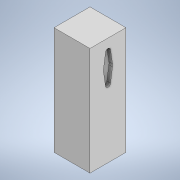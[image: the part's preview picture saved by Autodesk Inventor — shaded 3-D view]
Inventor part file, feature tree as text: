
AUTODESK INVENTOR PART (.ipt)
format: ipt  version: 2021 (Build 250183000, 183)  size: 110,080 bytes
history: native  units: mm
features: extrude x2, sketch x2
ambient origin geometry x8: Origin, YZ Plane, XZ Plane, XY Plane, X Axis, Y Axis, Z Axis, Center Point
bodies: Solid1 (feature_tree)
feature tree (4):
  extrude  "Extrusion1"  Depth=50.0mm
  extrude  "Extrusion2"  Depth=5.0mm
  sketch  "Sketch1"  dims[d0=50.0mm d1=50.0mm]
  sketch  "Sketch2"  dims[d2=150.0mm d3=0.0mm d4=13.0mm d5=7.0mm d6=20.0mm d7=5.0mm d8=0.0mm]
